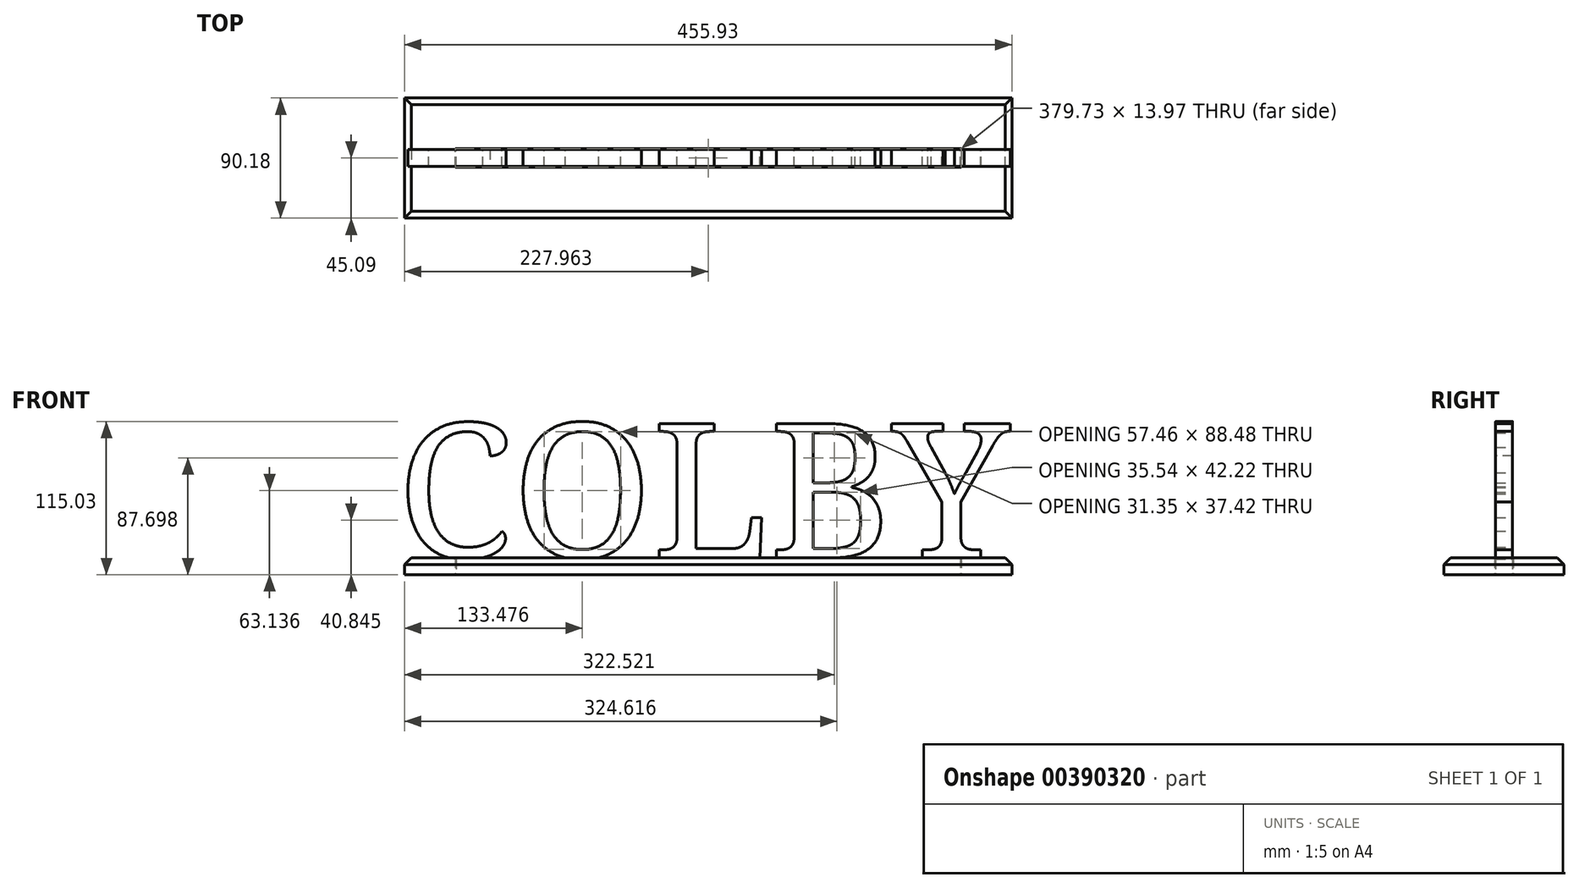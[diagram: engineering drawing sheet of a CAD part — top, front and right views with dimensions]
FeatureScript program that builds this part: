
annotation { "Feature Type Name" : "Feature", "Feature Type Description" : "" }
export const myFeature = defineFeature(function(context is Context, id is Id, definition is map)
    precondition{}
    {
        {
            var Q0;
            Q0=qCreatedBy(makeId("Front.planeOp"),FACE);
            var sketch = newSketch(context, id + "F0", { "sketchPlane" : qUnion([Q0])});
            skText(sketch, "E0", { "text": "COLBY", "fontName": "NotoSerif-Regular.ttf"});
            const initialGuessF0  = {"E0": [0, 0, 1, 0, 0.1016]};
            skSetInitialGuess(sketch, initialGuessF0);
            skSolve(sketch);
        }
        {
            var Q0;
            Q0 = qSketchRegion(id + "F0", true);
            extrude(context, id + "F1", {"entities" : qUnion([Q0]), "depth" : 12.7 * mm});
        }
        {
            var Q0;
            Q0=makeQuery(id+"F1.opExtrude","SWEPT_FACE",FACE,{"disambiguationData":[OSD([sQuery(id+"F0.wireOp",EDGE,"E0.sketch_text.stroke-201")])]});
            var sketch = newSketch(context, id + "F2", { "sketchPlane" : qUnion([Q0])});
            skLineSegment(sketch, "E1.bottom", {"start": v(-12.7, 0) * mm, "end": v(0, 0) * mm});
            skLineSegment(sketch, "E1.top", {"start": v(-12.7, -12.7) * mm, "end": v(0, -12.7) * mm});
            skLineSegment(sketch, "E1.left", {"start": v(-12.7, 0) * mm, "end": v(-12.7, -12.7) * mm});
            skLineSegment(sketch, "E1.right", {"start": v(0, 0) * mm, "end": v(0, -12.7) * mm});
            skSolve(sketch);
        }
        {
            var Q0;
            Q0 = qSketchRegion(id + "F2", true);
            extrude(context, id + "F3", {"entities" : qUnion([Q0]), "operationType" : NewBodyOperationType.ADD, "oppositeDirection" : true, "depth" : 393.7 * mm});
        }
        {
            var Q0;
            Q0=makeQuery(id+"F3.boolean.opBoolean","MERGE",FACE,{"derivedFrom":[makeQuery(id+"F1.opExtrude","SWEPT_FACE",FACE,{"disambiguationData":[OSD([sQuery(id+"F0.wireOp",EDGE,"E0.sketch_text.stroke-201")])]}),makeQuery(id+"F3.opExtrude","CAP_FACE",FACE,{"disambiguationData":[OSD([sQuery(id+"F2.wireOp",EDGE,"E1.bottom"),sQuery(id+"F2.wireOp",EDGE,"E1.top"),sQuery(id+"F2.wireOp",EDGE,"E1.left"),sQuery(id+"F2.wireOp",EDGE,"E1.right")])],"isStart":true})]});
            var sketch = newSketch(context, id + "F4", { "sketchPlane" : qUnion([Q0])});
            skLineSegment(sketch, "E2.bottom", {"start": v(-12.7, -12.7) * mm, "end": v(0, -12.7) * mm});
            skLineSegment(sketch, "E2.top", {"start": v(-12.7, 0) * mm, "end": v(0, 0) * mm});
            skLineSegment(sketch, "E2.left", {"start": v(-12.7, -12.7) * mm, "end": v(-12.7, 0) * mm});
            skLineSegment(sketch, "E2.right", {"start": v(0, -12.7) * mm, "end": v(0, 0) * mm});
            skSolve(sketch);
        }
        {
            var Q0;
            Q0 = qSketchRegion(id + "F4", true);
            extrude(context, id + "F5", {"entities" : qUnion([Q0]), "operationType" : NewBodyOperationType.REMOVE, "oppositeDirection" : true, "depth" : 15.24 * mm});
        }
        {
            var Q0;
            Q0=makeQuery(id+"F3.opExtrude","SWEPT_FACE",FACE,{"disambiguationData":[OSD([sQuery(id+"F2.wireOp",EDGE,"E1.top")])]});
            var sketch = newSketch(context, id + "F6", { "sketchPlane" : qUnion([Q0])});
            skLineSegment(sketch, "E3.0", {"start": v(423.26, -0.63) * mm, "end": v(423.26, 13.33) * mm});
            skLineSegment(sketch, "E3.1", {"start": v(43.53, -0.64) * mm, "end": v(423.26, -0.64) * mm});
            skLineSegment(sketch, "E3.2", {"start": v(43.53, 13.33) * mm, "end": v(43.53, -0.63) * mm});
            skLineSegment(sketch, "E3.3", {"start": v(423.26, 13.34) * mm, "end": v(43.53, 13.34) * mm});
            skLineSegment(sketch, "E4.0", {"start": v(461.36, 51.44) * mm, "end": v(5.43, 51.44) * mm});
            skLineSegment(sketch, "E4.1", {"start": v(461.36, -38.73) * mm, "end": v(461.36, 51.44) * mm});
            skLineSegment(sketch, "E4.2", {"start": v(5.43, -38.74) * mm, "end": v(461.36, -38.74) * mm});
            skLineSegment(sketch, "E4.3", {"start": v(5.43, 51.44) * mm, "end": v(5.43, -38.73) * mm});
            skSolve(sketch);
        }
        {
            var Q0;
            Q0 = qSketchRegion(id + "F6", true);
            extrude(context, id + "F7", {"entities" : qUnion([Q0]), "oppositeDirection" : true, "depth" : 12.7 * mm});
        }
        {
            var Q0;
            Q0=makeQuery(id+"F7.opExtrude","CAP_EDGE",EDGE,{"disambiguationData":[OSD([sQuery(id+"F6.wireOp",EDGE,"E4.0")])],"isStart":false});
            var Q1;
            Q1=makeQuery(id+"F7.opExtrude","CAP_EDGE",EDGE,{"disambiguationData":[OSD([sQuery(id+"F6.wireOp",EDGE,"E4.1")])],"isStart":false});
            var Q2;
            Q2=makeQuery(id+"F7.opExtrude","CAP_EDGE",EDGE,{"disambiguationData":[OSD([sQuery(id+"F6.wireOp",EDGE,"E4.2")])],"isStart":false});
            var Q3;
            Q3=makeQuery(id+"F7.opExtrude","CAP_EDGE",EDGE,{"disambiguationData":[OSD([sQuery(id+"F6.wireOp",EDGE,"E4.3")])],"isStart":false});
            chamfer(context, id + "F8", {"entities" : qUnion([Q0, Q1, Q2, Q3]), "width" : 5.08 * mm, "tangentPropagation" : true});
        }
    });
